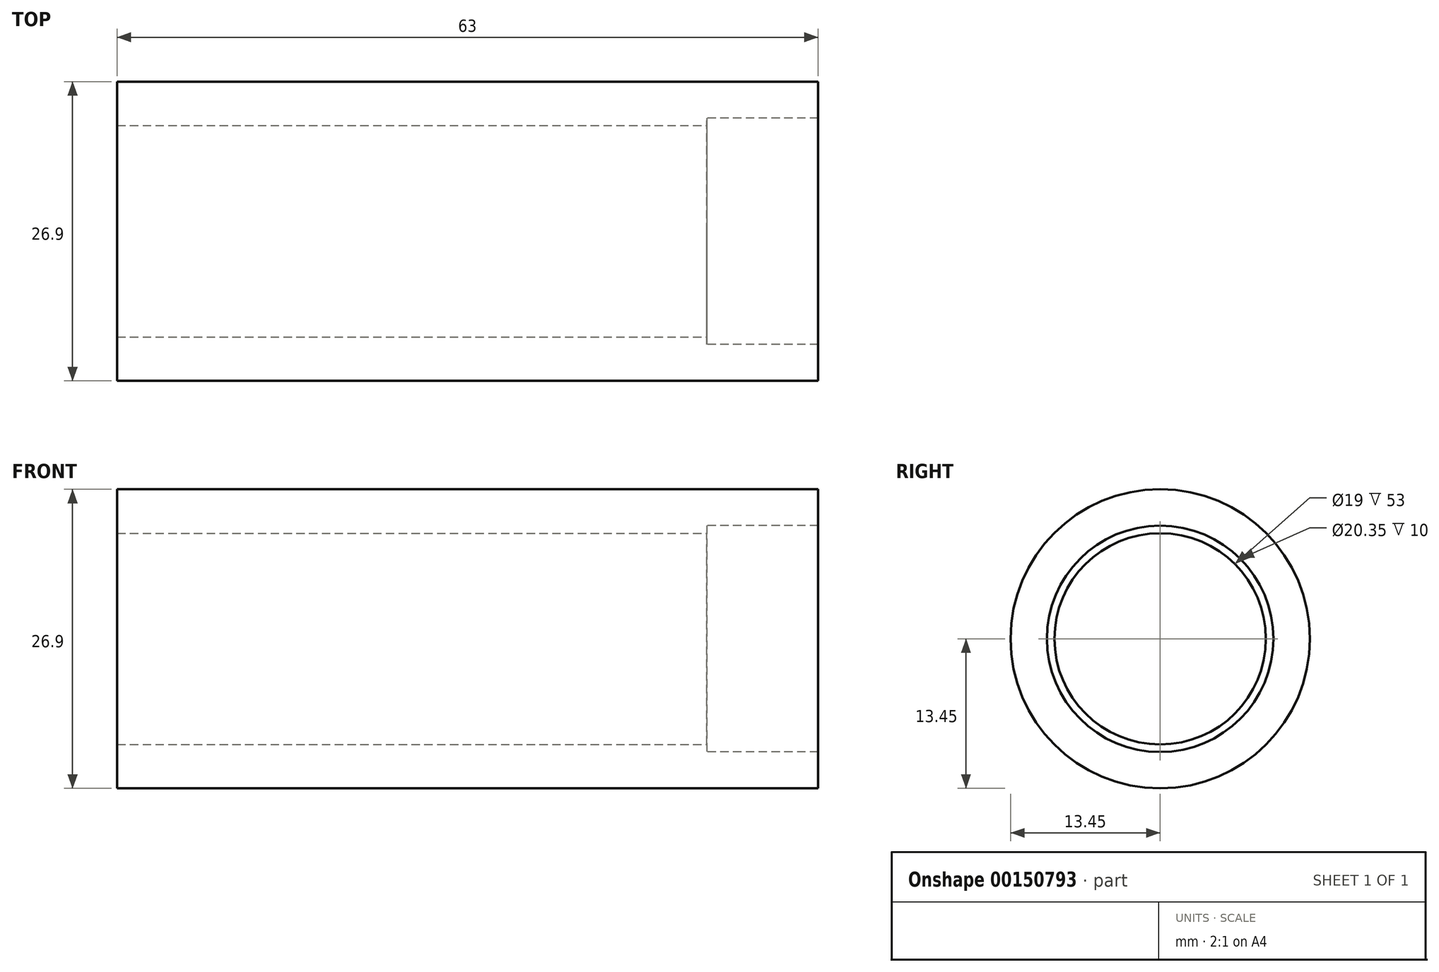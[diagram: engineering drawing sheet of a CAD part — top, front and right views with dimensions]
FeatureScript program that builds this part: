
annotation { "Feature Type Name" : "Feature", "Feature Type Description" : "" }
export const myFeature = defineFeature(function(context is Context, id is Id, definition is map)
    precondition{}
    {
        {
            var Q0;
            Q0=qCreatedBy(makeId("Right.planeOp"),FACE);
            var sketch = newSketch(context, id + "F0", { "sketchPlane" : qUnion([Q0])});
            skCircle(sketch, "E0", {"center": v(0, 0) * mm, "radius": 13.45 * mm});
            skCircle(sketch, "E1", {"center": v(0, 0) * mm, "radius": 9.5 * mm});
            skSolve(sketch);
        }
        {
            var Q0;
            Q0=qSketchRegion(id+"F0",true);
            extrude(context, id + "F1", {"entities" : qUnion([Q0]), "oppositeDirection" : true, "depth" : 63 * mm});
        }
        {
            var Q0;
            Q0=qCreatedBy(makeId("Front.planeOp"),FACE);
            var sketch = newSketch(context, id + "F2", { "sketchPlane" : qUnion([Q0])});
            skLineSegment(sketch, "E2.0", {"start": v(-63, 13.45) * mm, "end": v(-63, -13.45) * mm, "construction": true});
            skLineSegment(sketch, "E3", {"start": v(-63, 13.45) * mm, "end": v(0, 13.45) * mm, "construction": true});
            skLineSegment(sketch, "E4.0", {"start": v(0, 13.45) * mm, "end": v(0, -13.45) * mm, "construction": true});
            skLineSegment(sketch, "E5", {"start": v(0, 9.38) * mm, "end": v(0, 10.18) * mm});
            skLineSegment(sketch, "E6", {"start": v(0, 10.18) * mm, "end": v(-10, 10.18) * mm});
            skLineSegment(sketch, "E7", {"start": v(-10, 10.18) * mm, "end": v(-10, 9.38) * mm});
            skLineSegment(sketch, "E8", {"start": v(-10, 9.38) * mm, "end": v(0, 9.38) * mm});
            skLineSegment(sketch, "E9", {"start": v(0.87, 9.38) * mm, "end": v(-67.94, 9.38) * mm, "construction": true});
            skSolve(sketch);
        }
        {
            var Q0;
            Q0=qSketchRegion(id+"F2",true);
            var Q1;
            Q1=makeQuery(id+"F1.opExtrude","SWEPT_FACE",FACE,{"disambiguationData":[OSD([sQuery(id+"F0.wireOp",EDGE,"E1")])]});
            revolve(context, id + "F3", {"operationType" : NewBodyOperationType.REMOVE, "entities" : qUnion([Q0]), "axis" : qUnion([Q1]), "revolveType" : RevolveType.FULL, "oppositeDirection" : true});
        }
    });
